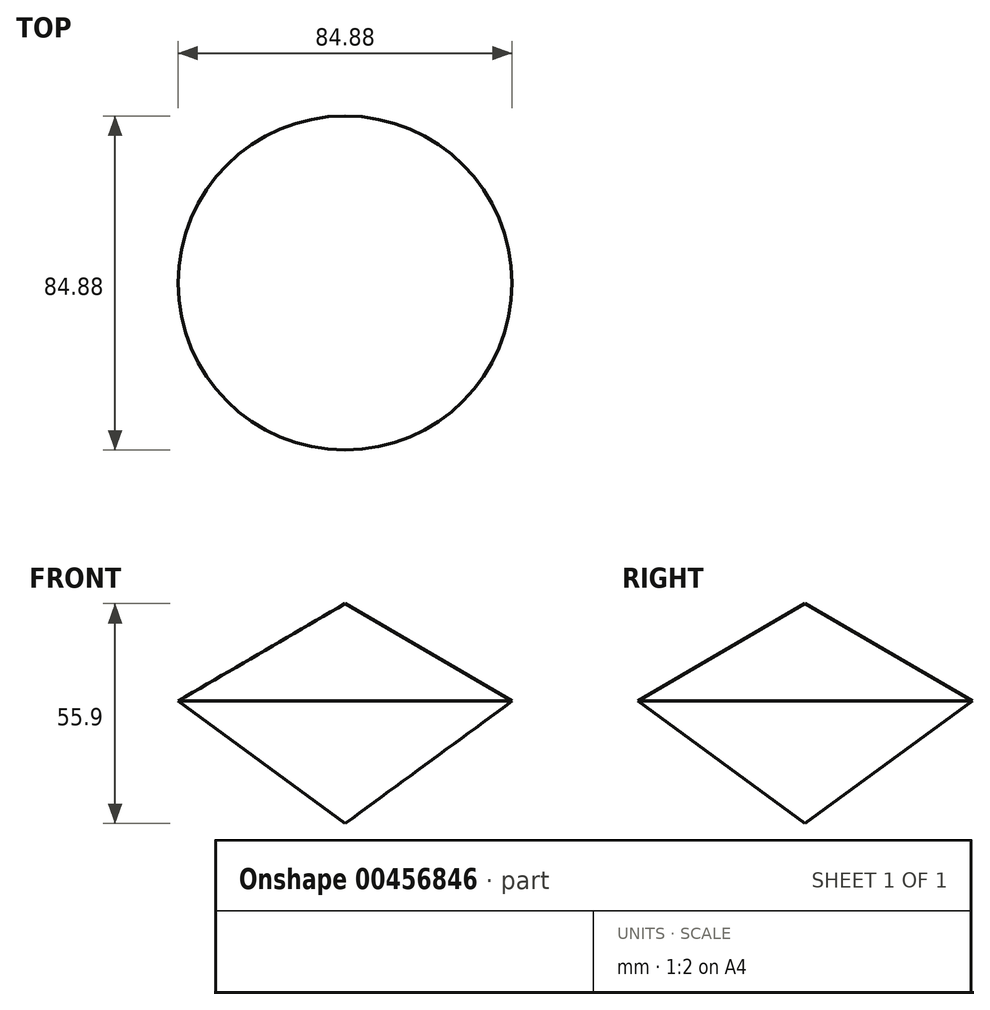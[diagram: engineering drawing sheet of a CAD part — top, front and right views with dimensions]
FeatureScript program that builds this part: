
annotation { "Feature Type Name" : "Feature", "Feature Type Description" : "" }
export const myFeature = defineFeature(function(context is Context, id is Id, definition is map)
    precondition{}
    {
        {
            var Q0;
            Q0=qCreatedBy(makeId("Front.planeOp"),FACE);
            var sketch = newSketch(context, id + "F0", { "sketchPlane" : qUnion([Q0])});
            skLineSegment(sketch, "E0", {"start": v(0, 0) * mm, "end": v(42.44, 31.1) * mm});
            skLineSegment(sketch, "E1", {"start": v(42.44, 31.1) * mm, "end": v(0, 55.9) * mm});
            skLineSegment(sketch, "E2", {"start": v(0, 55.9) * mm, "end": v(0, 0) * mm});
            skSolve(sketch);
        }
        {
            var Q0;
            Q0=makeQuery(id+"F0.imprint","IMPRINT",FACE,{"disambiguationData":[TD([[makeQuery(id+"F0.imprint","IMPRINT",EDGE,{"derivedFrom":sQuery(id+"F0.wireOp",EDGE,"E0")}),1.0]])]});
            var Q1;
            Q1=sQuery(id+"F0.wireOp",EDGE,"E2");
            revolve(context, id + "F1", {"entities" : qUnion([Q0]), "axis" : qUnion([Q1]), "revolveType" : RevolveType.FULL});
        }
    });
